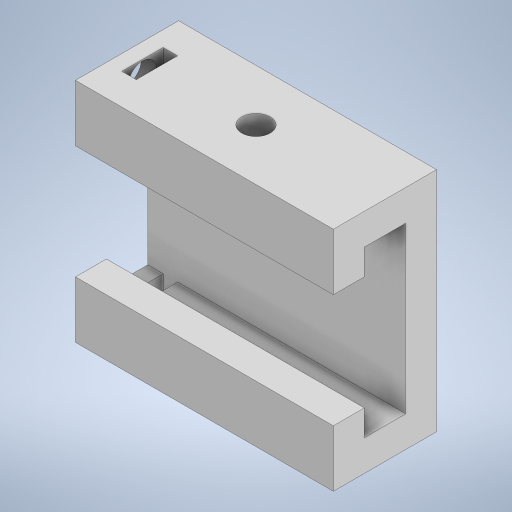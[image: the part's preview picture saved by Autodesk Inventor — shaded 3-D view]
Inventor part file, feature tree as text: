
AUTODESK INVENTOR PART (.ipt)
format: ipt  version: 2023.2 (Build 272271030, 271C)  size: 265,728 bytes
history: native  units: mm
features: extrude x4, sketch x4, plane x2, projected_geometry x1
ambient origin geometry x8: Origin, YZ Plane, XZ Plane, XY Plane, X Axis, Y Axis, Z Axis, Center Point
bodies: Solid1 (feature_tree)
feature tree (11):
  extrude  "Extrusion1"  Depth=32.0mm
  plane  "Work Plane1"
  extrude  "Extrusion2"  Depth=14.0mm
  extrude  "Extrusion3"  Depth=20.0mm
  plane  "Work Plane2"
  extrude  "Extrusion4"  Depth=22.0mm
  sketch  "Sketch1"  dims[d0=22.0mm d1=32.0mm]
  sketch  "Sketch2"  dims[d2=6.0mm d3=14.0mm]
  projected_geometry  "Projected Loop1"
  sketch  "Sketch3"  dims[d4=44.0mm d5=20.0mm]
  sketch  "Sketch4"  dims[d6=50.0mm d7=0.0mm d8=22.0mm d9=5.5mm d10=25.0mm d11=50.0mm d12=0.0mm d13=8.0mm d14=3.0mm d15=2.8mm d16=0.0mm d17=0.0mm d18=-25.0mm d19=5.5mm d20=19.0mm d21=10.0mm d22=0.0mm]
